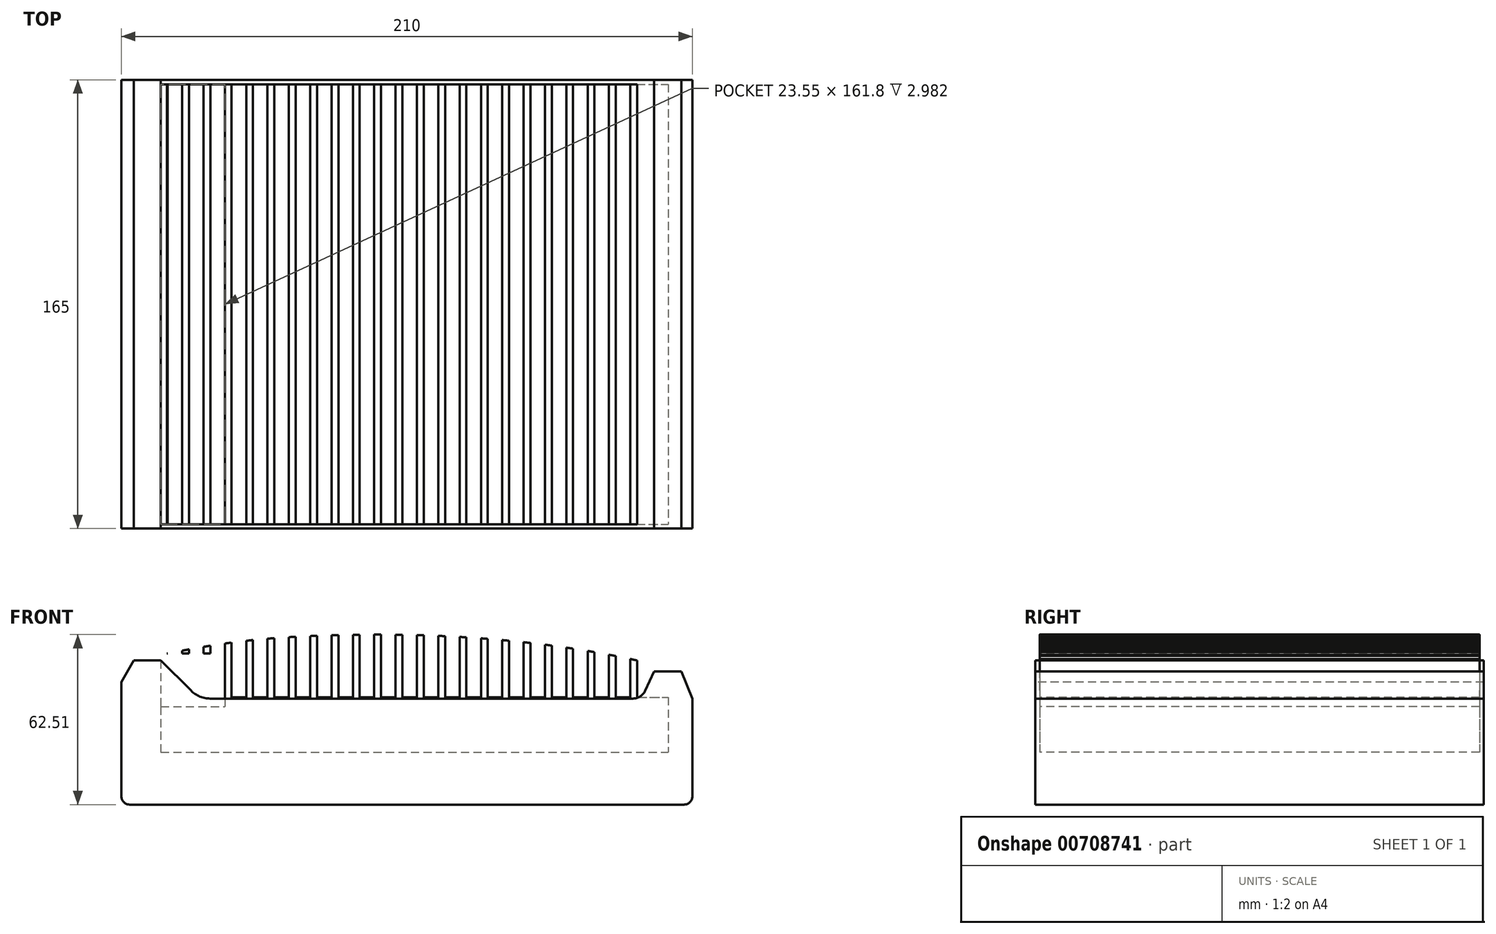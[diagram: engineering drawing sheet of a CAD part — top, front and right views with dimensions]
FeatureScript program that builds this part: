
annotation { "Feature Type Name" : "Feature", "Feature Type Description" : "" }
export const myFeature = defineFeature(function(context is Context, id is Id, definition is map)
    precondition{}
    {
        {
            var Q0;
            Q0=qCreatedBy(makeId("Front.planeOp"),FACE);
            var sketch = newSketch(context, id + "F0", { "sketchPlane" : qUnion([Q0])});
            skLineSegment(sketch, "E0.bottom", {"start": v(102, 0) * mm, "end": v(-102, 0) * mm});
            skLineSegment(sketch, "E0.right", {"start": v(-105, 3) * mm, "end": v(-105, 45) * mm});
            skPoint(sketch, "E0.middle", {"position": v(0, 22.5) * mm});
            skLineSegment(sketch, "E1", {"start": v(-105, 45) * mm, "end": v(-100.5, 53) * mm});
            skLineSegment(sketch, "E2", {"start": v(-100.5, 53) * mm, "end": v(-90.5, 53) * mm});
            skLineSegment(sketch, "E3", {"start": v(-90.5, 53) * mm, "end": v(-79.43, 41.93) * mm});
            skLineSegment(sketch, "E4", {"start": v(-72.36, 39) * mm, "end": v(83.15, 39) * mm});
            skLineSegment(sketch, "E5", {"start": v(87.68, 41.89) * mm, "end": v(91, 49) * mm});
            skLineSegment(sketch, "E6", {"start": v(91, 49) * mm, "end": v(101, 49) * mm});
            skLineSegment(sketch, "E7", {"start": v(101, 49) * mm, "end": v(105, 39) * mm});
            skLineSegment(sketch, "E8", {"start": v(105, 39) * mm, "end": v(105, 3) * mm});
            skPoint(sketch, "E9.visualSharp", {"position": v(-105, 0) * mm});
            skArc(sketch, "E9.filletArc", {"start": v(-105, 3) * mm, "mid": v(-104.12, 0.88) * mm, "end": v(-102, 0) * mm});
            skPoint(sketch, "E10.visualSharp", {"position": v(105, 0) * mm});
            skArc(sketch, "E10.filletArc", {"start": v(102, 0) * mm, "mid": v(104.12, 0.88) * mm, "end": v(105, 3) * mm});
            skPoint(sketch, "E11.visualSharp", {"position": v(-76.5, 39) * mm});
            skArc(sketch, "E11.filletArc", {"start": v(-79.43, 41.93) * mm, "mid": v(-76.18, 39.76) * mm, "end": v(-72.36, 39) * mm});
            skPoint(sketch, "E12.visualSharp", {"position": v(86.34, 39) * mm});
            skArc(sketch, "E12.filletArc", {"start": v(83.15, 39) * mm, "mid": v(85.84, 39.78) * mm, "end": v(87.68, 41.89) * mm});
            skSolve(sketch);
        }
        {
            var Q0;
            Q0 = qSketchRegion(id + "F0", true);
            extrude(context, id + "F1", {"entities" : qUnion([Q0]), "oppositeDirection" : true, "depth" : 165 * mm, "offsetDistance" : 25 * mm});
        }
        {
            var Q0;
            Q0=makeQuery(id+"F1.opExtrude","CAP_FACE",FACE,{"disambiguationData":[OSD([sQuery(id+"F0.wireOp",EDGE,"E0.bottom"),sQuery(id+"F0.wireOp",EDGE,"E0.right"),sQuery(id+"F0.wireOp",EDGE,"E1"),sQuery(id+"F0.wireOp",EDGE,"E2"),sQuery(id+"F0.wireOp",EDGE,"E3"),sQuery(id+"F0.wireOp",EDGE,"E4"),sQuery(id+"F0.wireOp",EDGE,"E5"),sQuery(id+"F0.wireOp",EDGE,"E6"),sQuery(id+"F0.wireOp",EDGE,"E7"),sQuery(id+"F0.wireOp",EDGE,"E8"),sQuery(id+"F0.wireOp",EDGE,"E9.filletArc"),sQuery(id+"F0.wireOp",EDGE,"E10.filletArc"),sQuery(id+"F0.wireOp",EDGE,"E11.filletArc"),sQuery(id+"F0.wireOp",EDGE,"E12.filletArc")])],"isStart":true});
            cPlane(context, id + "F2", {"entities" : qUnion([Q0]), "cplaneType" : CPlaneType.OFFSET, "offset" : 1.6 * mm, "oppositeDirection" : true, "width" : 150 * mm, "height" : 150 * mm});
        }
        {
            var Q0;
            Q0=qCreatedBy(id+"F2.planeOp",FACE);
            var sketch = newSketch(context, id + "F3", { "sketchPlane" : qUnion([Q0])});
            skFitSpline(sketch, "E13", {"points": [v(-100.5, 53) * mm, v(-35, 62) * mm, v(101, 49) * mm], "startDerivative": vector(211.57, 44.9) * mm, "endDerivative": vector(257.1, -70.4) * mm});
            skLineSegment(sketch, "E14.top", {"start": v(-100.5, 107.36) * mm, "end": v(101, 107.36) * mm});
            skLineSegment(sketch, "E14.left", {"start": v(-100.5, 53) * mm, "end": v(-100.5, 107.36) * mm});
            skLineSegment(sketch, "E14.right", {"start": v(101, 49) * mm, "end": v(101, 107.36) * mm});
            skSolve(sketch);
        }
        {
            var Q0;
            Q0=qCreatedBy(id+"F2.planeOp",FACE);
            var sketch = newSketch(context, id + "F4", { "sketchPlane" : qUnion([Q0])});
            skLineSegment(sketch, "E15.bottom", {"start": v(-90.5, 64) * mm, "end": v(-88, 64) * mm});
            skLineSegment(sketch, "E15.left", {"start": v(-90.5, 64) * mm, "end": v(-90.5, 39) * mm});
            skLineSegment(sketch, "E15.right", {"start": v(-88, 64) * mm, "end": v(-88, 39) * mm});
            skLineSegment(sketch, "E16.1.0.0", {"start": v(-80.15, 64) * mm, "end": v(-80.15, 39) * mm});
            skLineSegment(sketch, "E16.1.0.1", {"start": v(-82.65, 64) * mm, "end": v(-82.65, 39) * mm});
            skLineSegment(sketch, "E16.1.0.2", {"start": v(-82.65, 64) * mm, "end": v(-80.15, 64) * mm});
            skLineSegment(sketch, "E16.2.0.0", {"start": v(-72.3, 64) * mm, "end": v(-72.3, 39) * mm});
            skLineSegment(sketch, "E16.2.0.1", {"start": v(-74.8, 64) * mm, "end": v(-74.8, 39) * mm});
            skLineSegment(sketch, "E16.2.0.2", {"start": v(-74.8, 64) * mm, "end": v(-72.3, 64) * mm});
            skLineSegment(sketch, "E16.3.0.0", {"start": v(-64.45, 64) * mm, "end": v(-64.45, 39) * mm});
            skLineSegment(sketch, "E16.3.0.1", {"start": v(-66.95, 64) * mm, "end": v(-66.95, 39) * mm});
            skLineSegment(sketch, "E16.3.0.2", {"start": v(-66.95, 64) * mm, "end": v(-64.45, 64) * mm});
            skLineSegment(sketch, "E16.4.0.0", {"start": v(-56.6, 64) * mm, "end": v(-56.6, 39) * mm});
            skLineSegment(sketch, "E16.4.0.1", {"start": v(-59.1, 64) * mm, "end": v(-59.1, 39) * mm});
            skLineSegment(sketch, "E16.4.0.2", {"start": v(-59.1, 64) * mm, "end": v(-56.6, 64) * mm});
            skLineSegment(sketch, "E16.5.0.0", {"start": v(-48.75, 64) * mm, "end": v(-48.75, 39) * mm});
            skLineSegment(sketch, "E16.5.0.1", {"start": v(-51.25, 64) * mm, "end": v(-51.25, 39) * mm});
            skLineSegment(sketch, "E16.5.0.2", {"start": v(-51.25, 64) * mm, "end": v(-48.75, 64) * mm});
            skLineSegment(sketch, "E16.6.0.0", {"start": v(-40.9, 64) * mm, "end": v(-40.9, 39) * mm});
            skLineSegment(sketch, "E16.6.0.1", {"start": v(-43.4, 64) * mm, "end": v(-43.4, 39) * mm});
            skLineSegment(sketch, "E16.6.0.2", {"start": v(-43.4, 64) * mm, "end": v(-40.9, 64) * mm});
            skLineSegment(sketch, "E16.7.0.0", {"start": v(-33.05, 64) * mm, "end": v(-33.05, 39) * mm});
            skLineSegment(sketch, "E16.7.0.1", {"start": v(-35.55, 64) * mm, "end": v(-35.55, 39) * mm});
            skLineSegment(sketch, "E16.7.0.2", {"start": v(-35.55, 64) * mm, "end": v(-33.05, 64) * mm});
            skLineSegment(sketch, "E16.8.0.0", {"start": v(-25.2, 64) * mm, "end": v(-25.2, 39) * mm});
            skLineSegment(sketch, "E16.8.0.1", {"start": v(-27.7, 64) * mm, "end": v(-27.7, 39) * mm});
            skLineSegment(sketch, "E16.8.0.2", {"start": v(-27.7, 64) * mm, "end": v(-25.2, 64) * mm});
            skLineSegment(sketch, "E16.9.0.0", {"start": v(-17.35, 64) * mm, "end": v(-17.35, 39) * mm});
            skLineSegment(sketch, "E16.9.0.1", {"start": v(-19.85, 64) * mm, "end": v(-19.85, 39) * mm});
            skLineSegment(sketch, "E16.9.0.2", {"start": v(-19.85, 64) * mm, "end": v(-17.35, 64) * mm});
            skLineSegment(sketch, "E16.10.0.0", {"start": v(-9.5, 64) * mm, "end": v(-9.5, 39) * mm});
            skLineSegment(sketch, "E16.10.0.1", {"start": v(-12, 64) * mm, "end": v(-12, 39) * mm});
            skLineSegment(sketch, "E16.10.0.2", {"start": v(-12, 64) * mm, "end": v(-9.5, 64) * mm});
            skLineSegment(sketch, "E16.11.0.0", {"start": v(-1.65, 64) * mm, "end": v(-1.65, 39) * mm});
            skLineSegment(sketch, "E16.11.0.1", {"start": v(-4.15, 64) * mm, "end": v(-4.15, 39) * mm});
            skLineSegment(sketch, "E16.11.0.2", {"start": v(-4.15, 64) * mm, "end": v(-1.65, 64) * mm});
            skLineSegment(sketch, "E16.12.0.0", {"start": v(6.2, 64) * mm, "end": v(6.2, 39) * mm});
            skLineSegment(sketch, "E16.12.0.1", {"start": v(3.7, 64) * mm, "end": v(3.7, 39) * mm});
            skLineSegment(sketch, "E16.12.0.2", {"start": v(3.7, 64) * mm, "end": v(6.2, 64) * mm});
            skLineSegment(sketch, "E16.13.0.0", {"start": v(14.05, 64) * mm, "end": v(14.05, 39) * mm});
            skLineSegment(sketch, "E16.13.0.1", {"start": v(11.55, 64) * mm, "end": v(11.55, 39) * mm});
            skLineSegment(sketch, "E16.13.0.2", {"start": v(11.55, 64) * mm, "end": v(14.05, 64) * mm});
            skLineSegment(sketch, "E16.14.0.0", {"start": v(21.9, 64) * mm, "end": v(21.9, 39) * mm});
            skLineSegment(sketch, "E16.14.0.1", {"start": v(19.4, 64) * mm, "end": v(19.4, 39) * mm});
            skLineSegment(sketch, "E16.14.0.2", {"start": v(19.4, 64) * mm, "end": v(21.9, 64) * mm});
            skLineSegment(sketch, "E16.15.0.0", {"start": v(29.75, 64) * mm, "end": v(29.75, 39) * mm});
            skLineSegment(sketch, "E16.15.0.1", {"start": v(27.25, 64) * mm, "end": v(27.25, 39) * mm});
            skLineSegment(sketch, "E16.15.0.2", {"start": v(27.25, 64) * mm, "end": v(29.75, 64) * mm});
            skLineSegment(sketch, "E16.16.0.0", {"start": v(37.6, 64) * mm, "end": v(37.6, 39) * mm});
            skLineSegment(sketch, "E16.16.0.1", {"start": v(35.1, 64) * mm, "end": v(35.1, 39) * mm});
            skLineSegment(sketch, "E16.16.0.2", {"start": v(35.1, 64) * mm, "end": v(37.6, 64) * mm});
            skLineSegment(sketch, "E16.17.0.0", {"start": v(45.45, 64) * mm, "end": v(45.45, 39) * mm});
            skLineSegment(sketch, "E16.17.0.1", {"start": v(42.95, 64) * mm, "end": v(42.95, 39) * mm});
            skLineSegment(sketch, "E16.17.0.2", {"start": v(42.95, 64) * mm, "end": v(45.45, 64) * mm});
            skLineSegment(sketch, "E16.18.0.0", {"start": v(53.3, 64) * mm, "end": v(53.3, 39) * mm});
            skLineSegment(sketch, "E16.18.0.1", {"start": v(50.8, 64) * mm, "end": v(50.8, 39) * mm});
            skLineSegment(sketch, "E16.18.0.2", {"start": v(50.8, 64) * mm, "end": v(53.3, 64) * mm});
            skLineSegment(sketch, "E16.19.0.0", {"start": v(61.15, 64) * mm, "end": v(61.15, 39) * mm});
            skLineSegment(sketch, "E16.19.0.1", {"start": v(58.65, 64) * mm, "end": v(58.65, 39) * mm});
            skLineSegment(sketch, "E16.19.0.2", {"start": v(58.65, 64) * mm, "end": v(61.15, 64) * mm});
            skLineSegment(sketch, "E16.20.0.0", {"start": v(69, 64) * mm, "end": v(69, 39) * mm});
            skLineSegment(sketch, "E16.20.0.1", {"start": v(66.5, 64) * mm, "end": v(66.5, 39) * mm});
            skLineSegment(sketch, "E16.20.0.2", {"start": v(66.5, 64) * mm, "end": v(69, 64) * mm});
            skLineSegment(sketch, "E16.21.0.0", {"start": v(76.85, 64) * mm, "end": v(76.85, 39) * mm});
            skLineSegment(sketch, "E16.21.0.1", {"start": v(74.35, 64) * mm, "end": v(74.35, 39) * mm});
            skLineSegment(sketch, "E16.21.0.2", {"start": v(74.35, 64) * mm, "end": v(76.85, 64) * mm});
            skLineSegment(sketch, "E16.22.0.0", {"start": v(84.7, 64) * mm, "end": v(84.7, 39) * mm});
            skLineSegment(sketch, "E16.22.0.1", {"start": v(82.2, 64) * mm, "end": v(82.2, 39) * mm});
            skLineSegment(sketch, "E16.22.0.2", {"start": v(82.2, 64) * mm, "end": v(84.7, 64) * mm});
            skLineSegment(sketch, "E16.direction1", {"start": v(-88, 39) * mm, "end": v(-82.65, 39) * mm, "construction": true});
            skLineSegment(sketch, "E17.bottom", {"start": v(-88, 39) * mm, "end": v(-74.8, 39) * mm});
            skLineSegment(sketch, "E17.top", {"start": v(-90.5, 18.8) * mm, "end": v(96.08, 18.8) * mm});
            skLineSegment(sketch, "E17.left", {"start": v(-90.5, 39) * mm, "end": v(-90.5, 18.8) * mm});
            skLineSegment(sketch, "E17.right", {"start": v(96.08, 39) * mm, "end": v(96.08, 18.8) * mm});
            skLineSegment(sketch, "E18.trimOffspring", {"start": v(84.7, 39) * mm, "end": v(96.08, 39) * mm});
            skLineSegment(sketch, "E19.trimOffspring", {"start": v(76.85, 39) * mm, "end": v(82.2, 39) * mm});
            skLineSegment(sketch, "E20.trimOffspring", {"start": v(69, 39) * mm, "end": v(74.35, 39) * mm});
            skLineSegment(sketch, "E21.trimOffspring", {"start": v(61.15, 39) * mm, "end": v(66.5, 39) * mm});
            skLineSegment(sketch, "E22.trimOffspring", {"start": v(53.3, 39) * mm, "end": v(58.65, 39) * mm});
            skLineSegment(sketch, "E23.trimOffspring", {"start": v(45.45, 39) * mm, "end": v(50.8, 39) * mm});
            skLineSegment(sketch, "E24.trimOffspring", {"start": v(37.6, 39) * mm, "end": v(42.95, 39) * mm});
            skLineSegment(sketch, "E25.trimOffspring", {"start": v(29.75, 39) * mm, "end": v(35.1, 39) * mm});
            skLineSegment(sketch, "E26.trimOffspring", {"start": v(21.9, 39) * mm, "end": v(27.25, 39) * mm});
            skLineSegment(sketch, "E27.trimOffspring", {"start": v(14.05, 39) * mm, "end": v(19.4, 39) * mm});
            skLineSegment(sketch, "E28.trimOffspring", {"start": v(6.2, 39) * mm, "end": v(11.55, 39) * mm});
            skLineSegment(sketch, "E29.trimOffspring", {"start": v(-1.65, 39) * mm, "end": v(3.7, 39) * mm});
            skLineSegment(sketch, "E30.trimOffspring", {"start": v(-9.5, 39) * mm, "end": v(-4.15, 39) * mm});
            skLineSegment(sketch, "E31.trimOffspring", {"start": v(-17.35, 39) * mm, "end": v(-12, 39) * mm});
            skLineSegment(sketch, "E32.trimOffspring", {"start": v(-25.2, 39) * mm, "end": v(-19.85, 39) * mm});
            skLineSegment(sketch, "E33.trimOffspring", {"start": v(-33.05, 39) * mm, "end": v(-27.7, 39) * mm});
            skLineSegment(sketch, "E34.trimOffspring", {"start": v(-40.9, 39) * mm, "end": v(-35.55, 39) * mm});
            skLineSegment(sketch, "E35.trimOffspring", {"start": v(-48.75, 39) * mm, "end": v(-43.4, 39) * mm});
            skLineSegment(sketch, "E36.trimOffspring", {"start": v(-56.6, 39) * mm, "end": v(-51.25, 39) * mm});
            skLineSegment(sketch, "E37.trimOffspring", {"start": v(-64.45, 39) * mm, "end": v(-59.1, 39) * mm});
            skLineSegment(sketch, "E38.trimOffspring", {"start": v(-72.3, 39) * mm, "end": v(-66.95, 39) * mm});
            skSolve(sketch);
        }
        {
            var Q0;
            Q0=makeQuery(id+"F1.opExtrude","CAP_FACE",FACE,{"disambiguationData":[OSD([sQuery(id+"F0.wireOp",EDGE,"E0.bottom"),sQuery(id+"F0.wireOp",EDGE,"E0.right"),sQuery(id+"F0.wireOp",EDGE,"E1"),sQuery(id+"F0.wireOp",EDGE,"E2"),sQuery(id+"F0.wireOp",EDGE,"E3"),sQuery(id+"F0.wireOp",EDGE,"E4"),sQuery(id+"F0.wireOp",EDGE,"E5"),sQuery(id+"F0.wireOp",EDGE,"E6"),sQuery(id+"F0.wireOp",EDGE,"E7"),sQuery(id+"F0.wireOp",EDGE,"E8"),sQuery(id+"F0.wireOp",EDGE,"E9.filletArc"),sQuery(id+"F0.wireOp",EDGE,"E10.filletArc"),sQuery(id+"F0.wireOp",EDGE,"E11.filletArc"),sQuery(id+"F0.wireOp",EDGE,"E12.filletArc")])],"isStart":false});
            cPlane(context, id + "F5", {"entities" : qUnion([Q0]), "cplaneType" : CPlaneType.OFFSET, "offset" : 1.6 * mm, "oppositeDirection" : true, "width" : 150 * mm, "height" : 150 * mm});
        }
        {
            var Q0;
            Q0 = qSketchRegion(id + "F4", true);
            var Q1;
            Q1=qCreatedBy(id+"F5.planeOp",FACE);
            extrude(context, id + "F6", {"entities" : qUnion([Q0]), "endBound" : BoundingType.UP_TO_SURFACE, "oppositeDirection" : true, "depth" : 25 * mm, "endBoundEntityFace" : qUnion([Q1]), "offsetDistance" : 25 * mm});
        }
        {
            var Q0;
            Q0=makeQuery(id+"F6.opExtrude","SWEPT_BODY",BODY,{"disambiguationData":[OSD([sQuery(id+"F4.wireOp",EDGE,"E15.bottom"),sQuery(id+"F4.wireOp",EDGE,"E15.left"),sQuery(id+"F4.wireOp",EDGE,"E15.right"),sQuery(id+"F4.wireOp",EDGE,"E16.1.0.0"),sQuery(id+"F4.wireOp",EDGE,"E16.1.0.1"),sQuery(id+"F4.wireOp",EDGE,"E16.1.0.2"),sQuery(id+"F4.wireOp",EDGE,"E16.2.0.0"),sQuery(id+"F4.wireOp",EDGE,"E16.2.0.1"),sQuery(id+"F4.wireOp",EDGE,"E16.2.0.2"),sQuery(id+"F4.wireOp",EDGE,"E16.3.0.0"),sQuery(id+"F4.wireOp",EDGE,"E16.3.0.1"),sQuery(id+"F4.wireOp",EDGE,"E16.3.0.2"),sQuery(id+"F4.wireOp",EDGE,"E16.4.0.0"),sQuery(id+"F4.wireOp",EDGE,"E16.4.0.1"),sQuery(id+"F4.wireOp",EDGE,"E16.4.0.2"),sQuery(id+"F4.wireOp",EDGE,"E16.5.0.0"),sQuery(id+"F4.wireOp",EDGE,"E16.5.0.1"),sQuery(id+"F4.wireOp",EDGE,"E16.5.0.2"),sQuery(id+"F4.wireOp",EDGE,"E16.6.0.0"),sQuery(id+"F4.wireOp",EDGE,"E16.6.0.1"),sQuery(id+"F4.wireOp",EDGE,"E16.6.0.2"),sQuery(id+"F4.wireOp",EDGE,"E16.7.0.0"),sQuery(id+"F4.wireOp",EDGE,"E16.7.0.1"),sQuery(id+"F4.wireOp",EDGE,"E16.7.0.2"),sQuery(id+"F4.wireOp",EDGE,"E16.8.0.0"),sQuery(id+"F4.wireOp",EDGE,"E16.8.0.1"),sQuery(id+"F4.wireOp",EDGE,"E16.8.0.2"),sQuery(id+"F4.wireOp",EDGE,"E16.9.0.0"),sQuery(id+"F4.wireOp",EDGE,"E16.9.0.1"),sQuery(id+"F4.wireOp",EDGE,"E16.9.0.2"),sQuery(id+"F4.wireOp",EDGE,"E16.10.0.0"),sQuery(id+"F4.wireOp",EDGE,"E16.10.0.1"),sQuery(id+"F4.wireOp",EDGE,"E16.10.0.2"),sQuery(id+"F4.wireOp",EDGE,"E16.11.0.0"),sQuery(id+"F4.wireOp",EDGE,"E16.11.0.1"),sQuery(id+"F4.wireOp",EDGE,"E16.11.0.2"),sQuery(id+"F4.wireOp",EDGE,"E16.12.0.0"),sQuery(id+"F4.wireOp",EDGE,"E16.12.0.1"),sQuery(id+"F4.wireOp",EDGE,"E16.12.0.2"),sQuery(id+"F4.wireOp",EDGE,"E16.13.0.0"),sQuery(id+"F4.wireOp",EDGE,"E16.13.0.1"),sQuery(id+"F4.wireOp",EDGE,"E16.13.0.2"),sQuery(id+"F4.wireOp",EDGE,"E16.14.0.0"),sQuery(id+"F4.wireOp",EDGE,"E16.14.0.1"),sQuery(id+"F4.wireOp",EDGE,"E16.14.0.2"),sQuery(id+"F4.wireOp",EDGE,"E16.15.0.0"),sQuery(id+"F4.wireOp",EDGE,"E16.15.0.1"),sQuery(id+"F4.wireOp",EDGE,"E16.15.0.2"),sQuery(id+"F4.wireOp",EDGE,"E16.16.0.0"),sQuery(id+"F4.wireOp",EDGE,"E16.16.0.1"),sQuery(id+"F4.wireOp",EDGE,"E16.16.0.2"),sQuery(id+"F4.wireOp",EDGE,"E16.17.0.0"),sQuery(id+"F4.wireOp",EDGE,"E16.17.0.1"),sQuery(id+"F4.wireOp",EDGE,"E16.17.0.2"),sQuery(id+"F4.wireOp",EDGE,"E16.18.0.0"),sQuery(id+"F4.wireOp",EDGE,"E16.18.0.1"),sQuery(id+"F4.wireOp",EDGE,"E16.18.0.2"),sQuery(id+"F4.wireOp",EDGE,"E16.19.0.0"),sQuery(id+"F4.wireOp",EDGE,"E16.19.0.1"),sQuery(id+"F4.wireOp",EDGE,"E16.19.0.2"),sQuery(id+"F4.wireOp",EDGE,"E16.20.0.0"),sQuery(id+"F4.wireOp",EDGE,"E16.20.0.1"),sQuery(id+"F4.wireOp",EDGE,"E16.20.0.2"),sQuery(id+"F4.wireOp",EDGE,"E16.21.0.0"),sQuery(id+"F4.wireOp",EDGE,"E16.21.0.1"),sQuery(id+"F4.wireOp",EDGE,"E16.21.0.2"),sQuery(id+"F4.wireOp",EDGE,"E16.22.0.0"),sQuery(id+"F4.wireOp",EDGE,"E16.22.0.1"),sQuery(id+"F4.wireOp",EDGE,"E16.22.0.2"),sQuery(id+"F4.wireOp",EDGE,"E17.bottom"),sQuery(id+"F4.wireOp",EDGE,"E17.top"),sQuery(id+"F4.wireOp",EDGE,"E17.left"),sQuery(id+"F4.wireOp",EDGE,"E17.right"),sQuery(id+"F4.wireOp",EDGE,"E18.trimOffspring"),sQuery(id+"F4.wireOp",EDGE,"E19.trimOffspring"),sQuery(id+"F4.wireOp",EDGE,"E20.trimOffspring"),sQuery(id+"F4.wireOp",EDGE,"E21.trimOffspring"),sQuery(id+"F4.wireOp",EDGE,"E22.trimOffspring"),sQuery(id+"F4.wireOp",EDGE,"E23.trimOffspring"),sQuery(id+"F4.wireOp",EDGE,"E24.trimOffspring"),sQuery(id+"F4.wireOp",EDGE,"E25.trimOffspring"),sQuery(id+"F4.wireOp",EDGE,"E26.trimOffspring"),sQuery(id+"F4.wireOp",EDGE,"E27.trimOffspring"),sQuery(id+"F4.wireOp",EDGE,"E28.trimOffspring"),sQuery(id+"F4.wireOp",EDGE,"E29.trimOffspring"),sQuery(id+"F4.wireOp",EDGE,"E30.trimOffspring"),sQuery(id+"F4.wireOp",EDGE,"E31.trimOffspring"),sQuery(id+"F4.wireOp",EDGE,"E32.trimOffspring"),sQuery(id+"F4.wireOp",EDGE,"E33.trimOffspring"),sQuery(id+"F4.wireOp",EDGE,"E34.trimOffspring"),sQuery(id+"F4.wireOp",EDGE,"E35.trimOffspring"),sQuery(id+"F4.wireOp",EDGE,"E36.trimOffspring"),sQuery(id+"F4.wireOp",EDGE,"E37.trimOffspring"),sQuery(id+"F4.wireOp",EDGE,"E38.trimOffspring")])]});
            var Q1;
            Q1=makeQuery(id+"F1.opExtrude","CAP_EDGE",EDGE,{"disambiguationData":[OSD([sQuery(id+"F0.wireOp",EDGE,"E0.right")])],"isStart":true});
            transform(context, id + "F7", {"entities" : qUnion([Q0]), "transformType" : TransformType.TRANSLATION_DISTANCE, "transformDirection" : qUnion([Q1]), "distance" : .5 * mm, "makeCopy" : false});
        }
        {
            var Q0;
            Q0 = qSketchRegion(id + "F3", true);
            extrude(context, id + "F8", {"entities" : qUnion([Q0]), "operationType" : NewBodyOperationType.REMOVE, "endBound" : BoundingType.THROUGH_ALL, "oppositeDirection" : true, "depth" : 25 * mm, "offsetDistance" : 25 * mm});
        }
        {
            var Q0;
            Q0=qCreatedBy(id+"F2.planeOp",FACE);
            var sketch = newSketch(context, id + "F9", { "sketchPlane" : qUnion([Q0])});
            skLineSegment(sketch, "E39.bottom", {"start": v(-90.5, 55.52) * mm, "end": v(-66.95, 55.52) * mm});
            skLineSegment(sketch, "E39.top", {"start": v(-90.5, 36.02) * mm, "end": v(-66.95, 36.02) * mm});
            skLineSegment(sketch, "E39.left", {"start": v(-90.5, 55.52) * mm, "end": v(-90.5, 36.02) * mm});
            skLineSegment(sketch, "E39.right", {"start": v(-66.95, 55.52) * mm, "end": v(-66.95, 36.02) * mm});
            skSolve(sketch);
        }
        {
            var Q0;
            Q0 = qSketchRegion(id + "F9", true);
            var Q1;
            Q1=qCreatedBy(id+"F5.planeOp",FACE);
            extrude(context, id + "F10", {"entities" : qUnion([Q0]), "operationType" : NewBodyOperationType.REMOVE, "endBound" : BoundingType.UP_TO_SURFACE, "oppositeDirection" : true, "depth" : 25 * mm, "endBoundEntityFace" : qUnion([Q1]), "offsetDistance" : 25 * mm});
        }
    });
